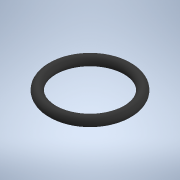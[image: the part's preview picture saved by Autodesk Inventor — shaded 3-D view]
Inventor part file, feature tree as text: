
AUTODESK INVENTOR PART (.ipt)
format: ipt  version: 2020.3 (Build 243373000, 373)  size: 129,024 bytes
history: native  units: mm
features: revolve x1, sketch x1
ambient origin geometry x8: Origin, YZ Plane, XZ Plane, XY Plane, X Axis, Y Axis, Z Axis, Center Point
bodies: Solid1 (feature_tree)
feature tree (2):
  revolve  "Revolution1"  [1 undecoded]
  sketch  "Sketch1"  dims[d0=1.8mm d1=7.11mm d2=90.0deg]
note: 1 required parameter value undecoded (feature->parameter linkage not recoverable at this tier; creation-order binding heuristic only, values carry confidence <= 0.55)
